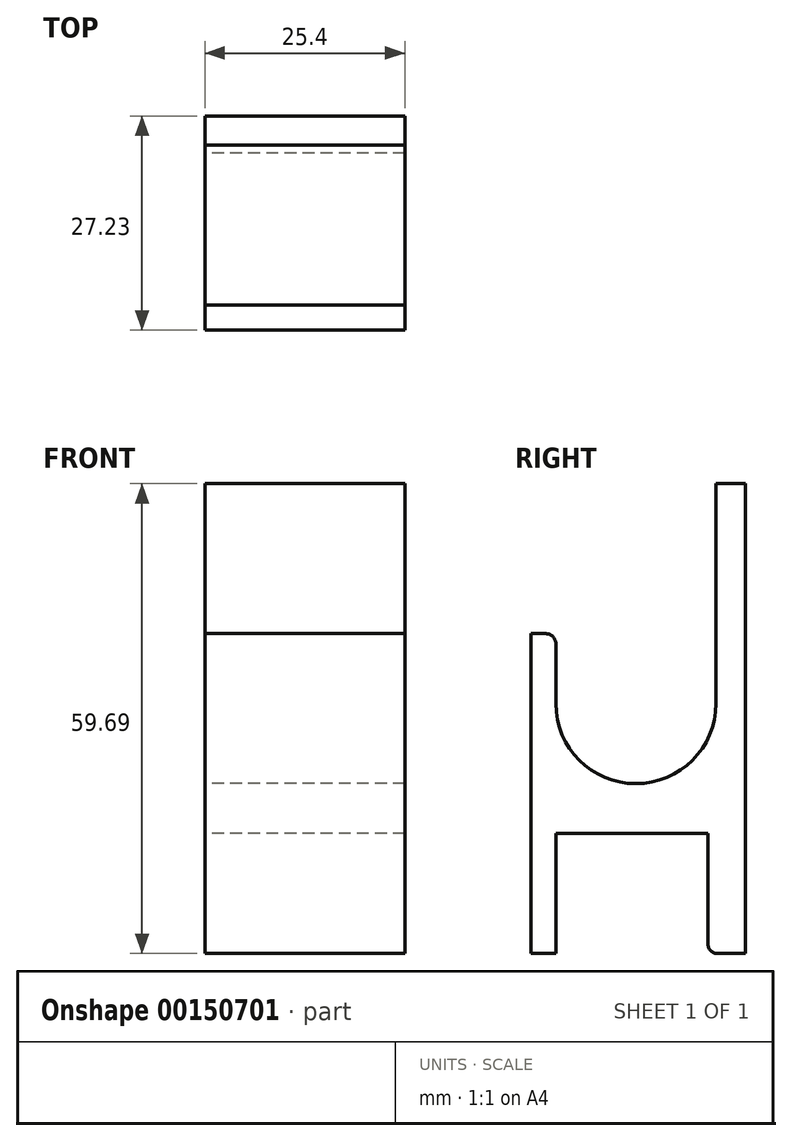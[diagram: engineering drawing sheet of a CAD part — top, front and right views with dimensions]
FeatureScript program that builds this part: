
annotation { "Feature Type Name" : "Feature", "Feature Type Description" : "" }
export const myFeature = defineFeature(function(context is Context, id is Id, definition is map)
    precondition{}
    {
        {
            var Q0;
            Q0=qCreatedBy(makeId("Right.planeOp"),FACE);
            var sketch = newSketch(context, id + "F0", { "sketchPlane" : qUnion([Q0])});
            skLineSegment(sketch, "E0", {"start": v(-24.03, 0) * mm, "end": v(-24.03, -15.24) * mm});
            skLineSegment(sketch, "E1", {"start": v(-26.08, -15.24) * mm, "end": v(-24.03, -15.24) * mm});
            skLineSegment(sketch, "E2", {"start": v(-24.03, 0) * mm, "end": v(-4.73, 0) * mm});
            skLineSegment(sketch, "E3", {"start": v(-4.73, 0) * mm, "end": v(-4.73, -15.24) * mm});
            skLineSegment(sketch, "E4", {"start": v(-4.73, -15.24) * mm, "end": v(0.02, -15.24) * mm});
            skLineSegment(sketch, "E5", {"start": v(0.02, -15.24) * mm, "end": v(0.02, 44.45) * mm});
            skLineSegment(sketch, "E6", {"start": v(-27.2, 25.4) * mm, "end": v(-24.03, 25.4) * mm});
            skLineSegment(sketch, "E7", {"start": v(-24.03, 25.4) * mm, "end": v(-24.03, 16.51) * mm});
            skLineSegment(sketch, "E8", {"start": v(-3.71, 16.51) * mm, "end": v(-3.71, 44.45) * mm});
            skLineSegment(sketch, "E9", {"start": v(-3.71, 44.45) * mm, "end": v(0.02, 44.45) * mm});
            skArc(sketch, "E10", {"start": v(-24.03, 16.51) * mm, "mid": v(-13.87, 6.35) * mm, "end": v(-3.71, 16.51) * mm});
            skLineSegment(sketch, "E11", {"start": v(-26.08, -15.24) * mm, "end": v(-27.2, -15.24) * mm});
            skLineSegment(sketch, "E12", {"start": v(-27.2, -15.24) * mm, "end": v(-27.2, 25.4) * mm});
            skSolve(sketch);
        }
        {
            var Q0;
            Q0=makeQuery(id+"F0.imprint","IMPRINT",FACE,{"disambiguationData":[TD([[makeQuery(id+"F0.imprint","IMPRINT",EDGE,{"derivedFrom":sQuery(id+"F0.wireOp",EDGE,"E0")}),-1.0]])]});
            extrude(context, id + "F1", {"entities" : qUnion([Q0]), "depth" : 25.4 * mm});
        }
        {
            var Q0;
            Q0=makeQuery(id+"F1.opExtrude","SWEPT_EDGE",EDGE,{"disambiguationData":[OSD([sQuery(id+"F0.wireOp",EDGE,"E6"),sQuery(id+"F0.wireOp",EDGE,"E7")])]});
            fillet(context, id + "F2", {"entities" : qUnion([Q0]), "radius" : 1.27 * mm, "tangentPropagation" : true, "allowEdgeOverflow" : false});
        }
        {
            var Q0;
            Q0=makeQuery(id+"F1.opExtrude","SWEPT_EDGE",EDGE,{"disambiguationData":[OSD([sQuery(id+"F0.wireOp",EDGE,"E3"),sQuery(id+"F0.wireOp",EDGE,"E4")])]});
            fillet(context, id + "F3", {"entities" : qUnion([Q0]), "radius" : 1.27 * mm, "tangentPropagation" : true, "allowEdgeOverflow" : false});
        }
    });
